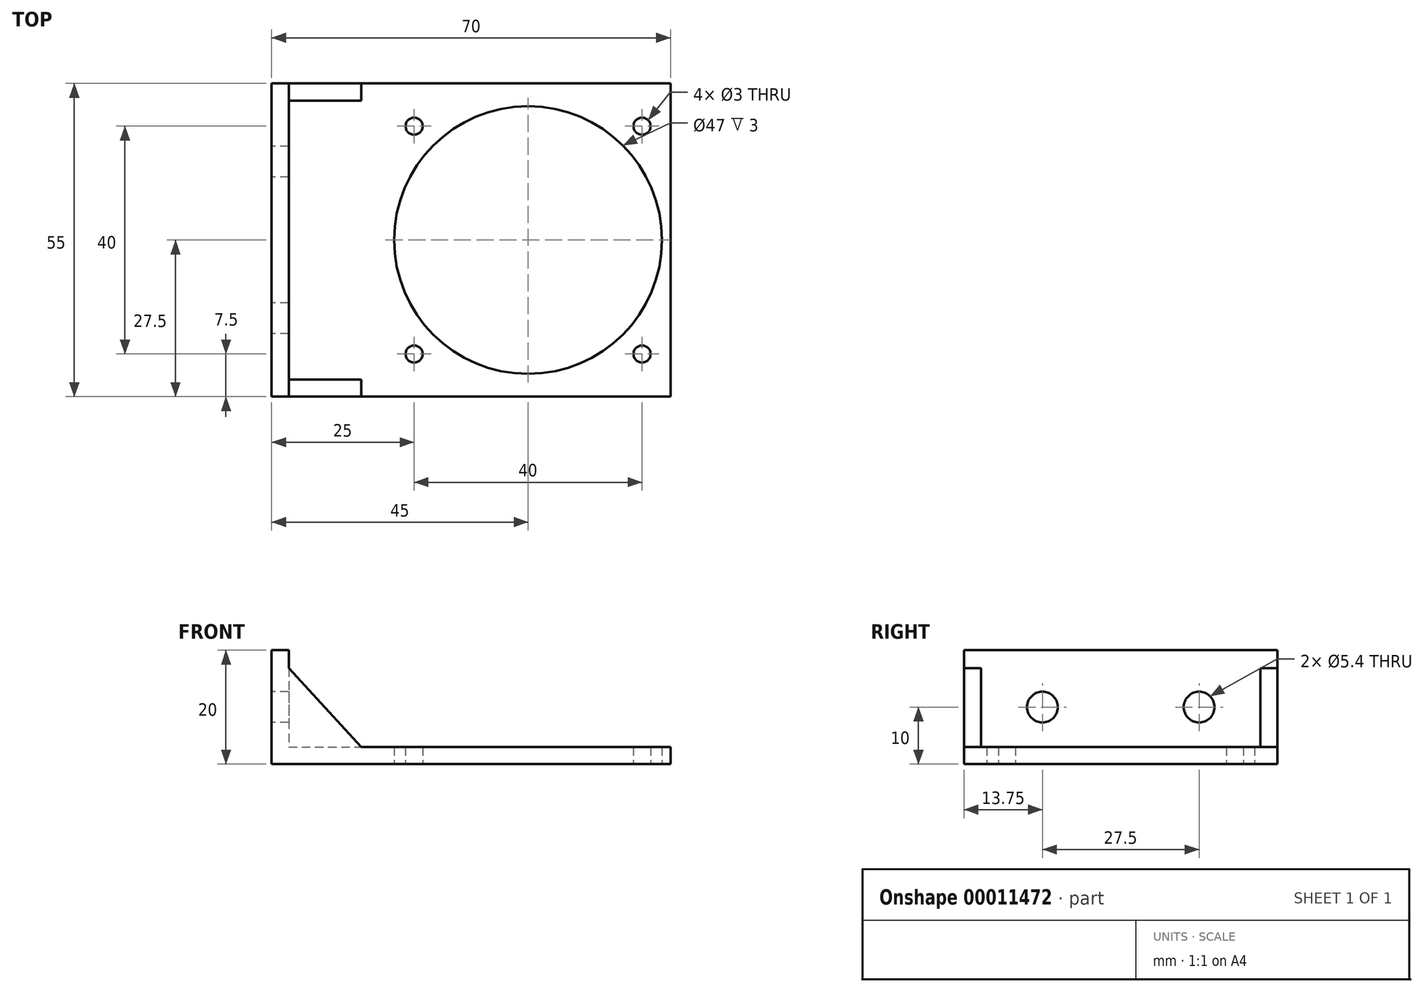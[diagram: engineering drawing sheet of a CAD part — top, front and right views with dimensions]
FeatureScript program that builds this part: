
annotation { "Feature Type Name" : "Feature", "Feature Type Description" : "" }
export const myFeature = defineFeature(function(context is Context, id is Id, definition is map)
    precondition{}
    {
        {
            var Q0;
            Q0=qCreatedBy(makeId("Top.planeOp"),FACE);
            var sketch = newSketch(context, id + "F0", { "sketchPlane" : qUnion([Q0])});
            skCircle(sketch, "E0", {"center": v(0, 0) * mm, "radius": 23.5 * mm});
            skLineSegment(sketch, "E1.bottom", {"start": v(-45, 27.5) * mm, "end": v(25, 27.5) * mm});
            skLineSegment(sketch, "E1.top", {"start": v(-45, -27.5) * mm, "end": v(25, -27.5) * mm});
            skLineSegment(sketch, "E1.left", {"start": v(-45, 27.5) * mm, "end": v(-45, -27.5) * mm});
            skLineSegment(sketch, "E1.right", {"start": v(25, 27.5) * mm, "end": v(25, -27.5) * mm});
            skCircle(sketch, "E2", {"center": v(20, 20) * mm, "radius": 1.5 * mm});
            skCircle(sketch, "E3.0.MirrorC", {"center": v(-20, 20) * mm, "radius": 1.5 * mm});
            skCircle(sketch, "E4.0.MirrorC", {"center": v(-20, -20) * mm, "radius": 1.5 * mm});
            skCircle(sketch, "E5.0.MirrorC", {"center": v(20, -20) * mm, "radius": 1.5 * mm});
            skSolve(sketch);
        }
        {
            var Q0;
            Q0 = qSketchRegion(id + "F0", true);
            extrude(context, id + "F1", {"entities" : qUnion([Q0]), "depth" : 3 * mm});
        }
        {
            var Q0;
            Q0=makeQuery(id+"F1.opExtrude","SWEPT_FACE",FACE,{"disambiguationData":[OSD([sQuery(id+"F0.wireOp",EDGE,"E1.left")])]});
            var sketch = newSketch(context, id + "F2", { "sketchPlane" : qUnion([Q0])});
            skLineSegment(sketch, "E6.bottom", {"start": v(-27.5, 0) * mm, "end": v(27.5, 0) * mm});
            skLineSegment(sketch, "E6.top", {"start": v(-27.5, 20) * mm, "end": v(27.5, 20) * mm});
            skLineSegment(sketch, "E6.left", {"start": v(-27.5, 0) * mm, "end": v(-27.5, 20) * mm});
            skLineSegment(sketch, "E6.right", {"start": v(27.5, 0) * mm, "end": v(27.5, 20) * mm});
            skLineSegment(sketch, "E7", {"start": v(-27.5, 10) * mm, "end": v(0, 10) * mm, "construction": true});
            skCircle(sketch, "E8", {"center": v(-13.75, 10) * mm, "radius": 2.7 * mm});
            skCircle(sketch, "E9.0.MirrorC", {"center": v(13.75, 10) * mm, "radius": 2.7 * mm});
            skSolve(sketch);
        }
        {
            var Q0;
            Q0 = qSketchRegion(id + "F2", true);
            extrude(context, id + "F3", {"entities" : qUnion([Q0]), "operationType" : NewBodyOperationType.ADD, "oppositeDirection" : true, "depth" : 3 * mm});
        }
        {
            var Q0;
            Q0=makeQuery(id+"F3.boolean.opBoolean","MERGE",FACE,{"derivedFrom":[makeQuery(id+"F1.opExtrude","SWEPT_FACE",FACE,{"disambiguationData":[OSD([sQuery(id+"F0.wireOp",EDGE,"E1.top")])]}),makeQuery(id+"F3.opExtrude","SWEPT_FACE",FACE,{"disambiguationData":[OSD([sQuery(id+"F2.wireOp",EDGE,"E6.right")])]})]});
            var sketch = newSketch(context, id + "F4", { "sketchPlane" : qUnion([Q0])});
            skLineSegment(sketch, "E10", {"start": v(-42, 3) * mm, "end": v(-42, 16.84) * mm});
            skLineSegment(sketch, "E11", {"start": v(-42, 16.84) * mm, "end": v(-29.26, 3) * mm});
            skLineSegment(sketch, "E12", {"start": v(-29.26, 3) * mm, "end": v(-42, 3) * mm});
            skSolve(sketch);
        }
        {
            var Q0;
            Q0 = qSketchRegion(id + "F4", true);
            extrude(context, id + "F5", {"entities" : qUnion([Q0]), "operationType" : NewBodyOperationType.ADD, "oppositeDirection" : true, "depth" : 3 * mm});
        }
        {
            var Q0;
            Q0=makeQuery(id+"F3.boolean.opBoolean","MERGE",FACE,{"derivedFrom":[makeQuery(id+"F1.opExtrude","SWEPT_FACE",FACE,{"disambiguationData":[OSD([sQuery(id+"F0.wireOp",EDGE,"E1.bottom")])]}),makeQuery(id+"F3.opExtrude","SWEPT_FACE",FACE,{"disambiguationData":[OSD([sQuery(id+"F2.wireOp",EDGE,"E6.left")])]})]});
            var sketch = newSketch(context, id + "F6", { "sketchPlane" : qUnion([Q0])});
            skLineSegment(sketch, "E13.0", {"start": v(42, 16.84) * mm, "end": v(29.26, 3) * mm});
            skLineSegment(sketch, "E14.0", {"start": v(42, 3) * mm, "end": v(-25, 3) * mm});
            skLineSegment(sketch, "E15.0", {"start": v(42, 20) * mm, "end": v(42, 3) * mm});
            skSolve(sketch);
        }
        {
            var Q0;
            Q0 = qSketchRegion(id + "F6", true);
            extrude(context, id + "F7", {"entities" : qUnion([Q0]), "operationType" : NewBodyOperationType.ADD, "oppositeDirection" : true, "depth" : 3 * mm});
        }
    });
